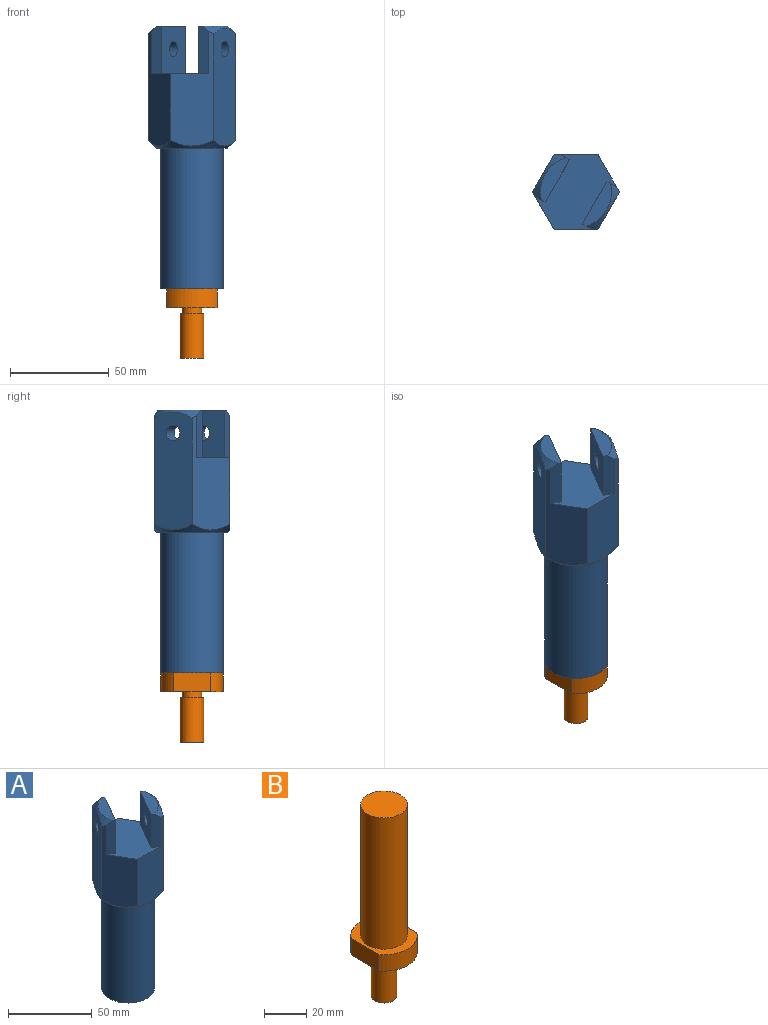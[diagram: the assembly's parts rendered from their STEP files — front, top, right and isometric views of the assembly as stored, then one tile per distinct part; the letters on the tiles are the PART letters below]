
ASSEMBLY  parts=2 mates=1
PART A: 27 faces, bbox 44.2x44.2x133 mm
  f0: plane 35.97x35.97mm, normal (0,0,-1), area 224.3mm2, adj f1,f5
  f1: cylinder r=15.88mm len=71.12mm, axis (0,0,1), area 7093.9mm2, adj f0,f2
  f2: plane 31.75x31.75mm, normal (0,0,-1), area 403.8mm2, adj f1,f3
  f3: cylinder r=11.11mm len=76.2mm, axis (0,0,-1), area 5313.3mm2, adj f2,f4,f25
  f4: plane 22.23x22.23mm, normal (0,0,-1), area 383.7mm2, adj f3,f25,f26
  f5: cone r=22mm half-angle=45deg, axis (0,0,1), area 337.1mm2, adj f0,f14,f15,f16,f17,f18,f19,f25
  f6: cylinder r=4mm len=11.04mm, axis (0.87,-0.5,0), area 204.3mm2, adj f9,f16
  f7: cylinder r=4mm len=11.04mm, axis (0.87,-0.5,0), area 204.3mm2, adj f8,f15
  f8: plane 24.13x21.45mm, normal (-0.87,0.5,0), area 547.3mm2, adj f7,f10,f13,f20,f21
  f9: plane 24.13x21.45mm, normal (0.87,-0.5,0), area 547.3mm2, adj f6,f10,f11,f12,f22
  f10: plane 41.23x38.1mm, normal (0,0,1), area 861.2mm2, adj f8,f9,f11,f13,f14,f17,f18,f19
  f11: plane 24.33x5.16mm, normal (-0.5,-0.87,0), area 133.4mm2, adj f9,f10,f12,f19,f23
  f12: plane 22.51x14.72mm, normal (0,0,1), area 136.6mm2, adj f9,f11,f22,f23
  f13: plane 24.33x5.16mm, normal (0.5,0.87,0), area 133.4mm2, adj f8,f10,f14,f21,f24
  f14: plane 58.03x19.18mm, normal (0.87,0.5,0), area 835.7mm2, adj f5,f10,f13,f15,f17,f24,f25
  f15: plane 59.6x19.05mm, normal (0.87,-0.5,0), area 1216.1mm2, adj f5,f7,f14,f18,f24
  f16: plane 59.6x19.05mm, normal (-0.87,0.5,0), area 1216.1mm2, adj f5,f6,f17,f19,f23
  f17: plane 58.03x22.14mm, normal (0,1,0), area 835.7mm2, adj f5,f10,f14,f16,f22,f23,f25
  f18: plane 58.03x22.16mm, normal (0,-1,0), area 838.7mm2, adj f5,f10,f15,f19,f20,f24
  f19: plane 58.03x19.18mm, normal (-0.87,-0.5,0), area 838.7mm2, adj f5,f10,f11,f16,f18,f23
  f20: plane 24.33x5.16mm, normal (-0.5,-0.87,0), area 133.4mm2, adj f8,f10,f18,f21,f24
  f21: plane 22.51x14.72mm, normal (0,0,1), area 136.6mm2, adj f8,f13,f20,f24
  f22: plane 24.33x5.16mm, normal (0.5,0.87,0), area 133.4mm2, adj f9,f10,f12,f17,f23
  f23: cone r=22mm half-angle=45deg, axis (0,0,-1), area 87.6mm2, adj f11,f12,f16,f17,f19,f22
  f24: cone r=22mm half-angle=45deg, axis (0,0,-1), area 87.6mm2, adj f13,f14,f15,f18,f20,f21
  f25: cylinder r=1.59mm len=12.59mm, axis (0.5,0.87,0), area 105.1mm2, adj f3,f4,f5,f14,f17,f26
  f26: plane 2.04x1.18mm, normal (0.5,0.87,0), area 0.8mm2, adj f4,f25
PART B: 12 faces, bbox 25.4x31.5x111.1 mm
  f0: cylinder r=15.75mm len=25.4mm, axis (0,0,1), area 281.4mm2, adj f2,f3,f10,f11
  f1: cylinder r=15.75mm len=25.4mm, axis (0,0,1), area 281.4mm2, adj f2,f3,f10,f11
  f2: plane 31.5x25.4mm, normal (0,0,-1), area 626.7mm2, adj f0,f1,f6,f10,f11
  f3: plane 31.5x25.4mm, normal (0,0,1), area 313.9mm2, adj f0,f1,f4,f10,f11
  f4: cylinder r=11.11mm len=76.2mm, axis (0,0,-1), area 5320.4mm2, adj f3,f5
  f5: plane 22.23x22.23mm, normal (0,0,1), area 387.9mm2, adj f4
  f6: cylinder r=4.89mm len=9.78mm, axis (0,0,1), area 85.8mm2, adj f2,f7
  f7: plane 12x12mm, normal (0,0,1), area 38mm2, adj f6,f9
  f8: plane 12x12mm, normal (0,0,-1), area 113.1mm2, adj f9
  f9: cylinder r=6mm len=22.61mm, axis (0,0,1), area 852.2mm2, adj f7,f8
  f10: plane 18.62x9.53mm, normal (-1,0,0), area 177.4mm2, adj f0,f1,f2,f3
  f11: plane 18.62x9.53mm, normal (1,0,0), area 177.4mm2, adj f0,f1,f2,f3
PLACE A t=(5.53,-2.23,34.29)mm fixed
PLACE B t=(5.53,-2.23,-36.83)mm
MATE slider B.f4 <-> A.f1  axis (0,0,-1) through (5.53,-2.23,1.27)mm
